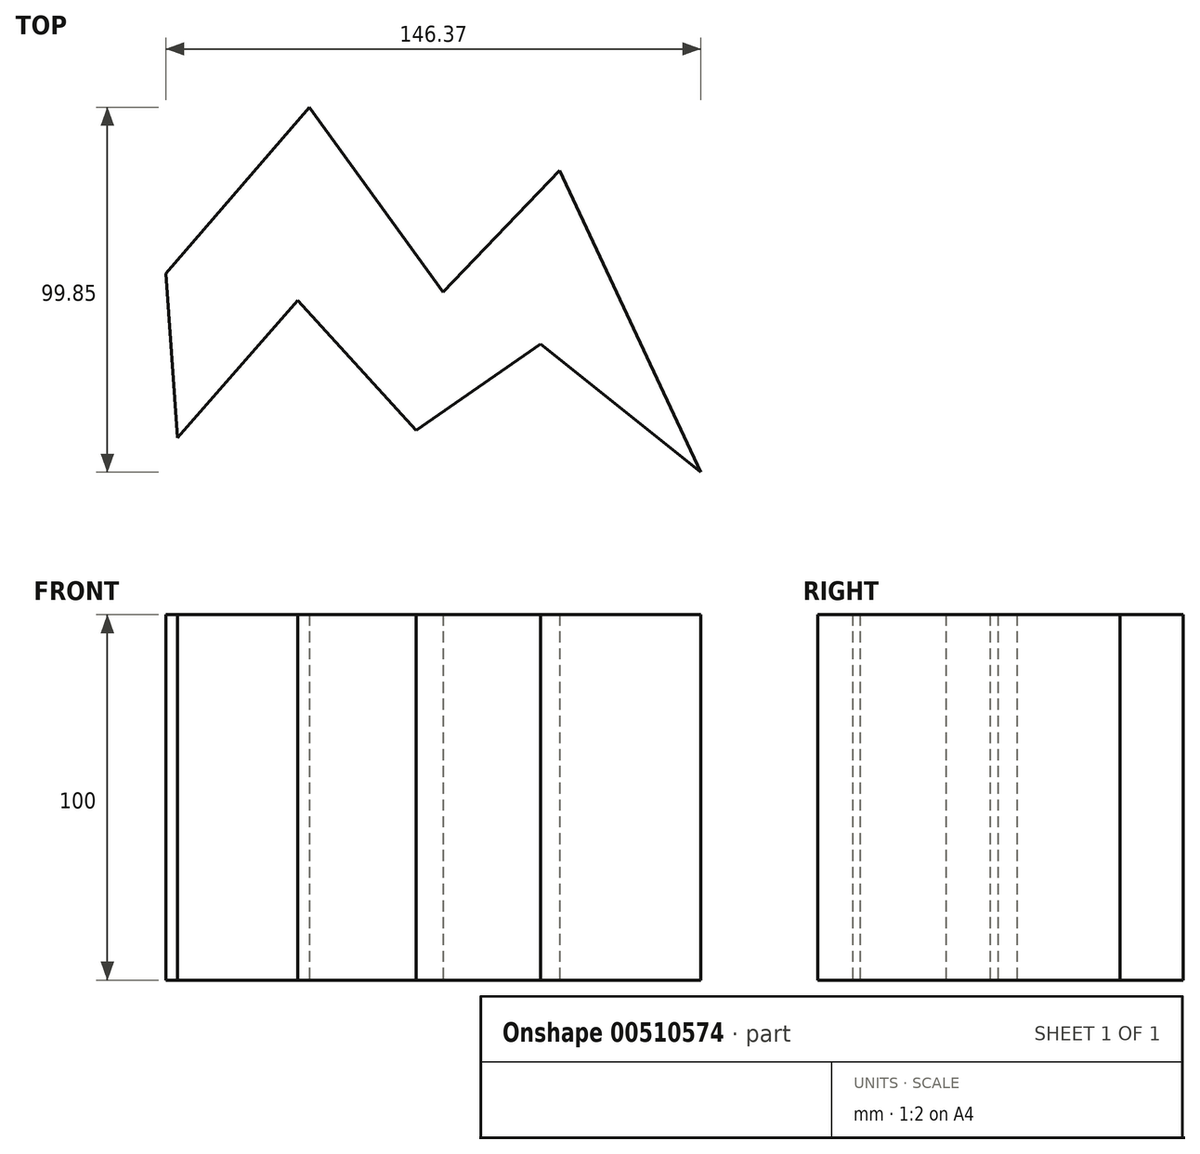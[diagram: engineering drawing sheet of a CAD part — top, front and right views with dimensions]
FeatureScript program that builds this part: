
annotation { "Feature Type Name" : "Feature", "Feature Type Description" : "" }
export const myFeature = defineFeature(function(context is Context, id is Id, definition is map)
    precondition{}
    {
        {
            var Q0;
            Q0=qCreatedBy(makeId("Top.planeOp"),FACE);
            var sketch = newSketch(context, id + "F0", { "sketchPlane" : qUnion([Q0])});
            skLineSegment(sketch, "E0", {"start": v(-47.55, 5.08) * mm, "end": v(-8.34, 50.56) * mm});
            skLineSegment(sketch, "E1", {"start": v(-8.34, 50.56) * mm, "end": v(28.25, 0) * mm});
            skLineSegment(sketch, "E2", {"start": v(28.25, 0) * mm, "end": v(60.14, 33.3) * mm});
            skLineSegment(sketch, "E3", {"start": v(60.14, 33.3) * mm, "end": v(98.82, -49.29) * mm});
            skLineSegment(sketch, "E4", {"start": v(98.82, -49.29) * mm, "end": v(54.9, -14.26) * mm});
            skLineSegment(sketch, "E5", {"start": v(54.9, -14.26) * mm, "end": v(20.93, -37.78) * mm});
            skLineSegment(sketch, "E6", {"start": v(20.93, -37.78) * mm, "end": v(-11.48, -2.24) * mm});
            skLineSegment(sketch, "E7", {"start": v(-11.48, -2.24) * mm, "end": v(-44.41, -39.88) * mm});
            skLineSegment(sketch, "E8", {"start": v(-44.41, -39.88) * mm, "end": v(-47.55, 5.08) * mm});
            skSolve(sketch);
        }
        {
            var Q0;
            Q0=makeQuery(id+"F0.imprint","IMPRINT",FACE,{"disambiguationData":[TD([[makeQuery(id+"F0.imprint","IMPRINT",EDGE,{"derivedFrom":sQuery(id+"F0.wireOp",EDGE,"E0")}),-1.0]])]});
            extrude(context, id + "F1", {"entities" : qUnion([Q0]), "depth" : 100 * mm});
        }
    });
